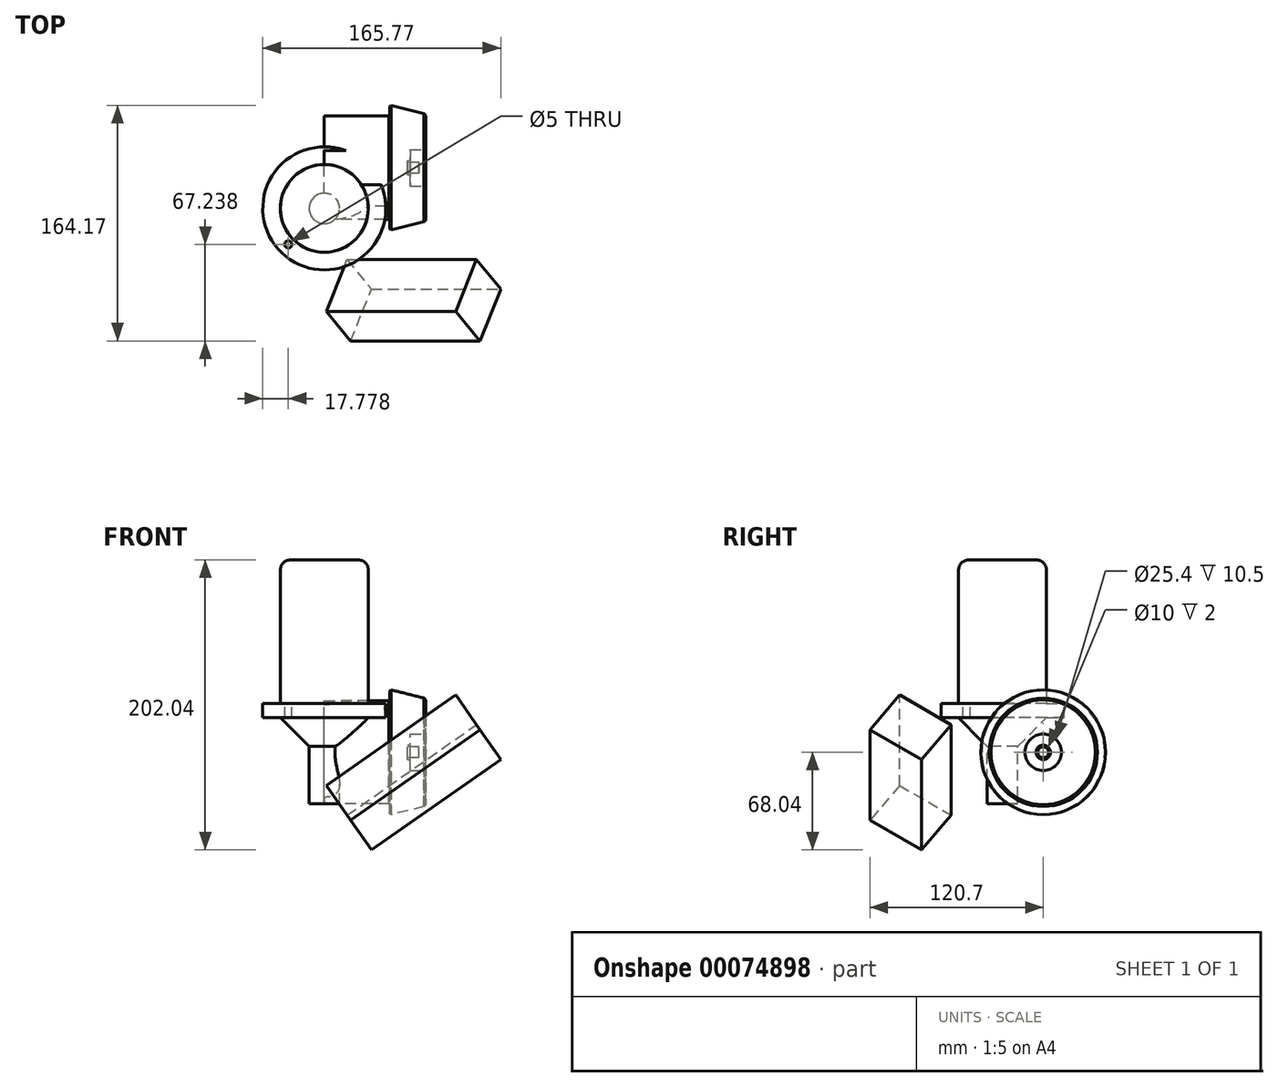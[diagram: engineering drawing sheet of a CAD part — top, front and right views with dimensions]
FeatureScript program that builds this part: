
annotation { "Feature Type Name" : "Feature", "Feature Type Description" : "" }
export const myFeature = defineFeature(function(context is Context, id is Id, definition is map)
    precondition{}
    {
        {
            var Q0;
            Q0=qCreatedBy(makeId("Top.planeOp"),FACE);
            var sketch = newSketch(context, id + "F0", { "sketchPlane" : qUnion([Q0])});
            skCircle(sketch, "E0", {"center": v(0, 0) * mm, "radius": 30.6 * mm});
            skLineSegment(sketch, "E1", {"start": v(0, 0) * mm, "end": v(25.1, 25.1) * mm, "construction": true});
            skCircle(sketch, "E2", {"center": v(25.1, 25.1) * mm, "radius": 2.5 * mm});
            skLineSegment(sketch, "E3", {"start": v(0, 0) * mm, "end": v(-25.1, -25.1) * mm, "construction": true});
            skCircle(sketch, "E4", {"center": v(-25.1, -25.1) * mm, "radius": 2.5 * mm});
            skCircle(sketch, "E5", {"center": v(0, 0) * mm, "radius": 42.88 * mm});
            skCircle(sketch, "E6", {"center": v(0, 0) * mm, "radius": 11.08 * mm});
            skLineSegment(sketch, "E7", {"start": v(0, 0) * mm, "end": v(28.59, 0) * mm, "construction": true});
            skSolve(sketch);
        }
        {
            var Q0;
            Q0=makeQuery(id+"F0.imprint","IMPRINT",FACE,{"disambiguationData":[TD([[makeQuery(id+"F0.imprint","IMPRINT",EDGE,{"derivedFrom":sQuery(id+"F0.wireOp",EDGE,"E0")}),1.0]])]});
            var Q1;
            Q1=makeQuery(id+"F0.imprint","IMPRINT",FACE,{"disambiguationData":[TD([[makeQuery(id+"F0.imprint","IMPRINT",EDGE,{"derivedFrom":sQuery(id+"F0.wireOp",EDGE,"E6")}),1.0]])]});
            extrude(context, id + "F1", {"entities" : qUnion([Q0, Q1]), "depth" : 100 * mm});
        }
        {
            var Q0;
            Q0=makeQuery(id+"F1.opExtrude","CAP_EDGE",EDGE,{"disambiguationData":[OSD([sQuery(id+"F0.wireOp",EDGE,"E0")])],"isStart":false});
            fillet(context, id + "F2", {"entities" : qUnion([Q0]), "radius" : 7 * mm, "tangentPropagation" : true, "allowEdgeOverflow" : false});
        }
        {
            var Q0;
            Q0 = qSketchRegion(id + "F0", true);
            extrude(context, id + "F3", {"entities" : qUnion([Q0]), "operationType" : NewBodyOperationType.ADD, "oppositeDirection" : true, "depth" : 10 * mm});
        }
        {
            var Q0;
            Q0=makeQuery(id+"F0.imprint","IMPRINT",FACE,{"disambiguationData":[TD([[makeQuery(id+"F0.imprint","IMPRINT",EDGE,{"derivedFrom":sQuery(id+"F0.wireOp",EDGE,"E6")}),1.0]])]});
            extrude(context, id + "F4", {"entities" : qUnion([Q0]), "operationType" : NewBodyOperationType.ADD, "oppositeDirection" : true, "depth" : 30 * mm});
        }
        {
            var Q0;
            Q0=makeQuery(id+"F0.imprint","IMPRINT",FACE,{"disambiguationData":[TD([[makeQuery(id+"F0.imprint","IMPRINT",EDGE,{"derivedFrom":sQuery(id+"F0.wireOp",EDGE,"E0")}),1.0]])]});
            extrude(context, id + "F5", {"entities" : qUnion([Q0]), "operationType" : NewBodyOperationType.ADD, "oppositeDirection" : true, "depth" : 30 * mm});
        }
        {
            var Q0;
            Q0=makeQuery(id+"F5.opExtrude","CAP_EDGE",EDGE,{"disambiguationData":[OSD([sQuery(id+"F0.wireOp",EDGE,"E0")])],"isStart":false});
            chamfer(context, id + "F6", {"entities" : qUnion([Q0]), "width" : 20 * mm, "tangentPropagation" : true});
        }
        {
            var Q0;
            {var subQ0=sQuery(id+"F0.wireOp",EDGE,"E6");Q0=makeQuery(id+"F5.boolean.opBoolean","MERGE",FACE,{"derivedFrom":[makeQuery(id+"F4.opExtrude","CAP_FACE",FACE,{"disambiguationData":[OSD([subQ0])],"isStart":false}),makeQuery(id+"F5.opExtrude","CAP_FACE",FACE,{"disambiguationData":[OSD([sQuery(id+"F0.wireOp",EDGE,"E0"),subQ0])],"isStart":false})]});}
            extrude(context, id + "F7", {"entities" : qUnion([Q0]), "operationType" : NewBodyOperationType.ADD, "depth" : 40 * mm});
        }
        {
            var Q0;
            Q0=qCreatedBy(makeId("Right.planeOp"),FACE);
            var sketch = newSketch(context, id + "F8", { "sketchPlane" : qUnion([Q0])});
            skCircle(sketch, "E8", {"center": v(28.36, -34) * mm, "radius": 36 * mm});
            skCircle(sketch, "E9", {"center": v(28.36, -34) * mm, "radius": 12.7 * mm});
            skCircle(sketch, "E10", {"center": v(28.36, -34) * mm, "radius": 5 * mm});
            skCircle(sketch, "E11", {"center": v(28.36, -34) * mm, "radius": 3.8 * mm});
            skSolve(sketch);
        }
        {
            var Q0;
            Q0=makeQuery(id+"F8.imprint","IMPRINT",FACE,{"disambiguationData":[TD([[makeQuery(id+"F8.imprint","IMPRINT",EDGE,{"derivedFrom":sQuery(id+"F8.wireOp",EDGE,"E8")}),1.0]])]});
            extrude(context, id + "F9", {"entities" : qUnion([Q0]), "operationType" : NewBodyOperationType.ADD, "depth" : 45 * mm});
        }
        {
            var Q0;
            Q0=makeQuery(id+"F8.imprint","IMPRINT",FACE,{"disambiguationData":[TD([[makeQuery(id+"F8.imprint","IMPRINT",EDGE,{"derivedFrom":sQuery(id+"F8.wireOp",EDGE,"E9")}),1.0]])]});
            extrude(context, id + "F10", {"entities" : qUnion([Q0]), "operationType" : NewBodyOperationType.ADD, "depth" : (45 + 9) * mm});
        }
        {
            var Q0;
            Q0=makeQuery(id+"F8.imprint","IMPRINT",FACE,{"disambiguationData":[TD([[makeQuery(id+"F8.imprint","IMPRINT",EDGE,{"derivedFrom":sQuery(id+"F8.wireOp",EDGE,"E10")}),1.0]])]});
            var Q1;
            Q1=makeQuery(id+"F8.imprint","IMPRINT",FACE,{"disambiguationData":[TD([[makeQuery(id+"F8.imprint","IMPRINT",EDGE,{"derivedFrom":sQuery(id+"F8.wireOp",EDGE,"E11")}),1.0]])]});
            var Q2;
            Q2=sQuery(id+"F8.wireOp",EDGE,"E10");
            extrude(context, id + "F11", {"entities" : qUnion([Q0, Q1]), "operationType" : NewBodyOperationType.ADD, "surfaceEntities" : qUnion([Q2]), "depth" : (52 + 6) * mm});
        }
        {
            var Q0;
            Q0=makeQuery(id+"F8.imprint","IMPRINT",FACE,{"disambiguationData":[TD([[makeQuery(id+"F8.imprint","IMPRINT",EDGE,{"derivedFrom":sQuery(id+"F8.wireOp",EDGE,"E11")}),1.0]])]});
            extrude(context, id + "F12", {"entities" : qUnion([Q0]), "operationType" : NewBodyOperationType.ADD, "depth" : (58 + 8) * mm});
        }
        {
            var Q0;
            Q0=makeQuery(id+"F11.opExtrude","CAP_FACE",FACE,{"disambiguationData":[OSD([sQuery(id+"F8.wireOp",EDGE,"E10")])],"isStart":false});
            var sketch = newSketch(context, id + "F13", { "sketchPlane" : qUnion([Q0])});
            skCircle(sketch, "E12", {"center": v(28.36, -34) * mm, "radius": 4.5 * mm});
            skCircle(sketch, "E13", {"center": v(28.36, -34) * mm, "radius": 12.7 * mm});
            skCircle(sketch, "E14", {"center": v(28.36, -34) * mm, "radius": 45 * mm});
            skSolve(sketch);
        }
        {
            var Q0;
            Q0=makeQuery(id+"F13.imprint","IMPRINT",FACE,{"disambiguationData":[TD([[makeQuery(id+"F13.imprint","IMPRINT",EDGE,{"derivedFrom":sQuery(id+"F13.wireOp",EDGE,"E13")}),1.0]])]});
            extrude(context, id + "F14", {"entities" : qUnion([Q0]), "oppositeDirection" : true, "depth" : 4 * mm, "hasSecondDirection" : true, "secondDirectionOppositeDirection" : false, "secondDirectionDepth" : 2 * mm});
        }
        {
            var Q0;
            Q0=makeQuery(id+"F13.imprint","IMPRINT",FACE,{"disambiguationData":[TD([[makeQuery(id+"F13.imprint","IMPRINT",EDGE,{"derivedFrom":sQuery(id+"F13.wireOp",EDGE,"E12")}),-1.0]])]});
            extrude(context, id + "F15", {"entities" : qUnion([Q0]), "operationType" : NewBodyOperationType.ADD, "oppositeDirection" : true, "depth" : 4 * mm});
        }
        {
            var Q0;
            Q0=makeQuery(id+"F13.imprint","IMPRINT",FACE,{"disambiguationData":[TD([[makeQuery(id+"F13.imprint","IMPRINT",EDGE,{"derivedFrom":sQuery(id+"F13.wireOp",EDGE,"E13")}),-1.0]])]});
            extrude(context, id + "F16", {"entities" : qUnion([Q0]), "operationType" : NewBodyOperationType.ADD, "oppositeDirection" : true, "depth" : 12.33 * mm, "hasSecondDirection" : true, "secondDirectionOppositeDirection" : false, "secondDirectionDepth" : 12.5 * mm});
        }
        {
            var Q0;
            Q0=makeQuery(id+"F16.opExtrude","CAP_EDGE",EDGE,{"disambiguationData":[OSD([sQuery(id+"F13.wireOp",EDGE,"E14")])],"isStart":true});
            chamfer(context, id + "F17", {"entities" : qUnion([Q0]), "chamferType" : ChamferType.TWO_OFFSETS, "width1" : 7.5 * mm, "oppositeDirection" : false, "width2" : 30 * mm});
        }
        {
            var Q0;
            {var subQ0=sQuery(id+"F13.wireOp",EDGE,"E14");Q0=makeQuery(id+"F17.opChamfer","BLEND_EDGE",EDGE,{"blendedFrom":[makeQuery(id+"F16.opExtrude","CAP_EDGE",EDGE,{"disambiguationData":[OSD([subQ0])],"isStart":true}),makeQuery(id+"F16.opExtrude","CAP_FACE",FACE,{"disambiguationData":[OSD([sQuery(id+"F13.wireOp",EDGE,"E13"),subQ0])],"isStart":true})],"blendedInto":[makeQuery(id+"F16.opExtrude","CAP_FACE",FACE,{"disambiguationData":[OSD([sQuery(id+"F13.wireOp",EDGE,"E13"),subQ0])],"isStart":true})]});}
            var Q1;
            {var subQ0=sQuery(id+"F13.wireOp",EDGE,"E14");Q1=makeQuery(id+"F17.opChamfer","BLEND_EDGE",EDGE,{"blendedFrom":[makeQuery(id+"F16.opExtrude","CAP_EDGE",EDGE,{"disambiguationData":[OSD([subQ0])],"isStart":true}),makeQuery(id+"F16.opExtrude","CAP_FACE",FACE,{"disambiguationData":[OSD([sQuery(id+"F13.wireOp",EDGE,"E13"),subQ0])],"isStart":false})],"blendedInto":[makeQuery(id+"F16.opExtrude","CAP_FACE",FACE,{"disambiguationData":[OSD([sQuery(id+"F13.wireOp",EDGE,"E13"),subQ0])],"isStart":false})]});}
            chamfer(context, id + "F18", {"entities" : qUnion([Q0, Q1]), "width" : 1 * mm, "tangentPropagation" : true});
        }
        {
            var Q0;
            Q0=qCreatedBy(makeId("Top.planeOp"),FACE);
            var sketch = newSketch(context, id + "F19", { "sketchPlane" : qUnion([Q0])});
            skLineSegment(sketch, "E15.bottom", {"start": v(-59.45, -78.8) * mm, "end": v(50.55, -78.8) * mm});
            skLineSegment(sketch, "E15.top", {"start": v(-59.45, -114.8) * mm, "end": v(50.55, -114.8) * mm});
            skLineSegment(sketch, "E15.left", {"start": v(-59.45, -78.8) * mm, "end": v(-59.45, -114.8) * mm});
            skLineSegment(sketch, "E15.right", {"start": v(50.55, -78.8) * mm, "end": v(50.55, -114.8) * mm});
            skSolve(sketch);
        }
        {
            var Q0;
            Q0=makeQuery(id+"F19.imprint","IMPRINT",FACE,{"disambiguationData":[TD([[makeQuery(id+"F19.imprint","IMPRINT",EDGE,{"derivedFrom":sQuery(id+"F19.wireOp",EDGE,"E15.bottom")}),-1.0]])]});
            extrude(context, id + "F20", {"entities" : qUnion([Q0]), "depth" : 44 * mm});
        }
        {
            var Q0;
            Q0=makeQuery(id+"F20.opExtrude","SWEPT_BODY",BODY,{"disambiguationData":[OSD([sQuery(id+"F19.wireOp",EDGE,"E15.bottom"),sQuery(id+"F19.wireOp",EDGE,"E15.top"),sQuery(id+"F19.wireOp",EDGE,"E15.left"),sQuery(id+"F19.wireOp",EDGE,"E15.right")])]});
            var Q1;
            Q1=makeQuery(id+"F20.opExtrude","CAP_EDGE",EDGE,{"disambiguationData":[OSD([sQuery(id+"F19.wireOp",EDGE,"E15.left")])],"isStart":false});
            transform(context, id + "F21", {"entities" : qUnion([Q0]), "transformType" : TransformType.ROTATION, "transformAxis" : qUnion([Q1]), "angle" : 35 * degree, "makeCopy" : false});
        }
        {
            var Q0;
            Q0=makeQuery(id+"F20.opExtrude","SWEPT_BODY",BODY,{"disambiguationData":[OSD([sQuery(id+"F19.wireOp",EDGE,"E15.bottom"),sQuery(id+"F19.wireOp",EDGE,"E15.top"),sQuery(id+"F19.wireOp",EDGE,"E15.left"),sQuery(id+"F19.wireOp",EDGE,"E15.right")])]});
            var Q1;
            Q1=makeQuery(id+"F20.opExtrude","CAP_EDGE",EDGE,{"disambiguationData":[OSD([sQuery(id+"F19.wireOp",EDGE,"E15.top")])],"isStart":true});
            transform(context, id + "F22", {"entities" : qUnion([Q0]), "transformType" : TransformType.ROTATION, "transformAxis" : qUnion([Q1]), "angle" : 55 * degree, "makeCopy" : false});
        }
        {
            var Q0;
            Q0=makeQuery(id+"F20.opExtrude","SWEPT_BODY",BODY,{"disambiguationData":[OSD([sQuery(id+"F19.wireOp",EDGE,"E15.bottom"),sQuery(id+"F19.wireOp",EDGE,"E15.top"),sQuery(id+"F19.wireOp",EDGE,"E15.left"),sQuery(id+"F19.wireOp",EDGE,"E15.right")])]});
            transform(context, id + "F23", {"entities" : qUnion([Q0]), "transformType" : TransformType.TRANSLATION_3D, "dx" : 67 * mm, "dy" : 58.5 * mm, "dz" : -110 * mm, "makeCopy" : false});
        }
    });
